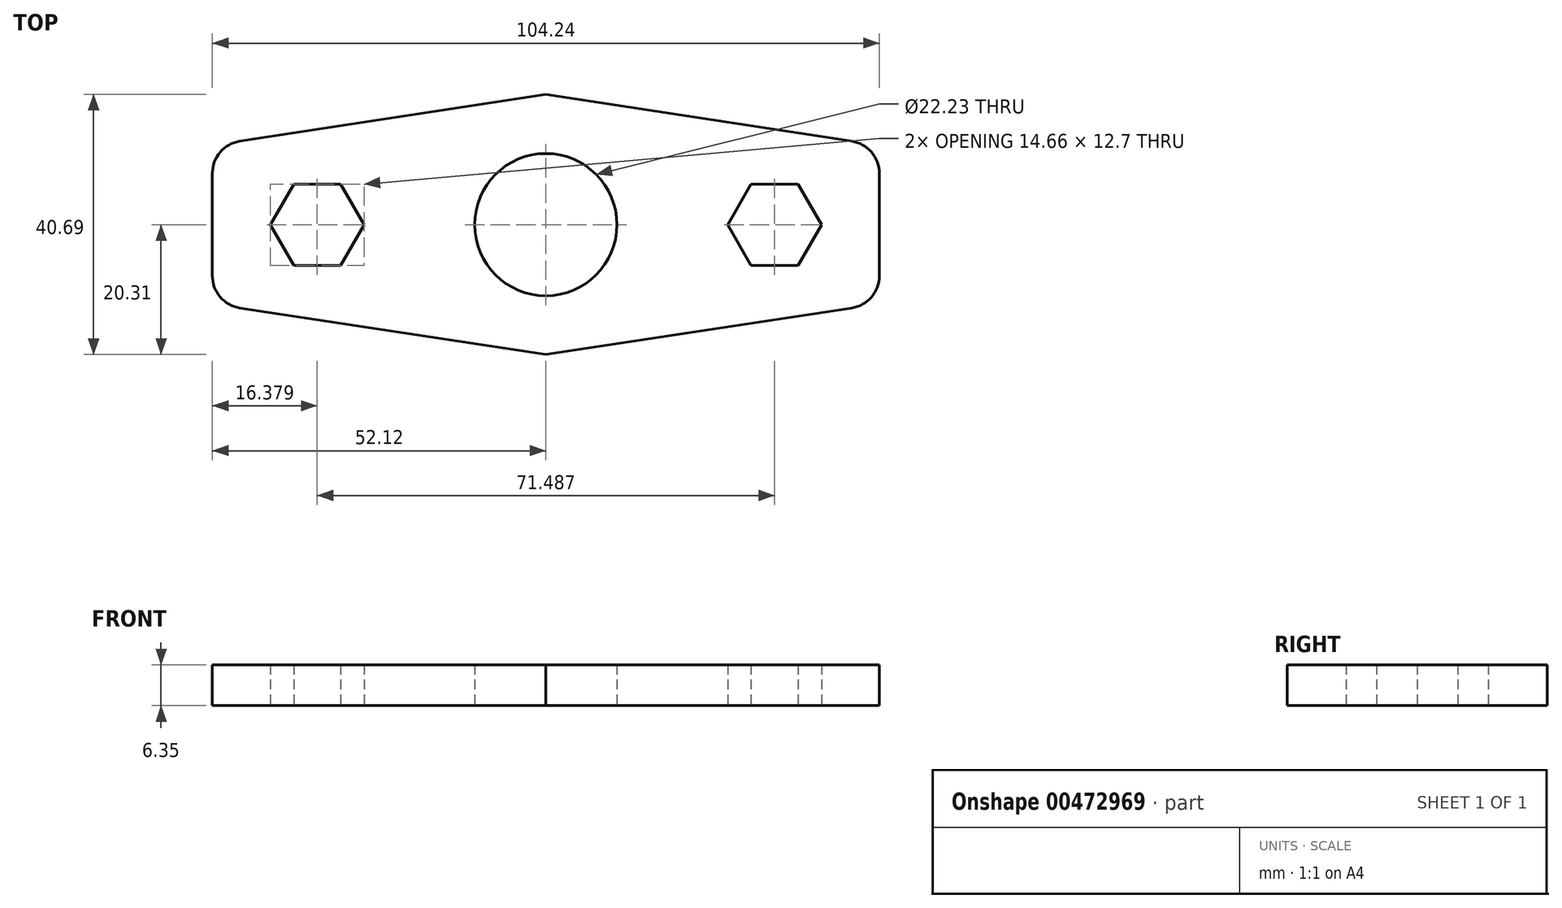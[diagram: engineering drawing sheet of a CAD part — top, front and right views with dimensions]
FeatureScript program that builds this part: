
annotation { "Feature Type Name" : "Feature", "Feature Type Description" : "" }
export const myFeature = defineFeature(function(context is Context, id is Id, definition is map)
    precondition{}
    {
        {
            var Q0;
            Q0=qCreatedBy(makeId("Top.planeOp"),FACE);
            var sketch = newSketch(context, id + "F0", { "sketchPlane" : qUnion([Q0])});
            skCircle(sketch, "E0.cCircle", {"center": v(-35.74, 0) * mm, "radius": 6.35 * mm, "construction": true});
            skLineSegment(sketch, "E0.0", {"start": v(-39.4, 6.35) * mm, "end": v(-32.08, 6.35) * mm});
            skLineSegment(sketch, "E0.1", {"start": v(-32.08, 6.35) * mm, "end": v(-28.4, 0) * mm});
            skLineSegment(sketch, "E0.2", {"start": v(-28.4, 0) * mm, "end": v(-32.08, -6.35) * mm});
            skLineSegment(sketch, "E0.3", {"start": v(-32.08, -6.35) * mm, "end": v(-39.4, -6.35) * mm});
            skLineSegment(sketch, "E0.4", {"start": v(-39.4, -6.35) * mm, "end": v(-43.07, 0) * mm});
            skLineSegment(sketch, "E0.5", {"start": v(-43.07, 0) * mm, "end": v(-39.4, 6.35) * mm});
            skPoint(sketch, "E0.0.midPoint", {"position": v(-35.74, 6.35) * mm});
            skCircle(sketch, "E1.cCircle", {"center": v(35.75, 0) * mm, "radius": 6.35 * mm, "construction": true});
            skLineSegment(sketch, "E1.0", {"start": v(32.08, 6.35) * mm, "end": v(39.41, 6.35) * mm});
            skLineSegment(sketch, "E1.1", {"start": v(39.41, 6.35) * mm, "end": v(43.08, 0) * mm});
            skLineSegment(sketch, "E1.2", {"start": v(43.08, 0) * mm, "end": v(39.41, -6.35) * mm});
            skLineSegment(sketch, "E1.3", {"start": v(39.41, -6.35) * mm, "end": v(32.08, -6.35) * mm});
            skLineSegment(sketch, "E1.4", {"start": v(32.08, -6.35) * mm, "end": v(28.41, 0) * mm});
            skLineSegment(sketch, "E1.5", {"start": v(28.41, 0) * mm, "end": v(32.08, 6.35) * mm});
            skPoint(sketch, "E1.0.midPoint", {"position": v(35.75, 6.35) * mm});
            skCircle(sketch, "E2", {"center": v(0, 0) * mm, "radius": 11.11 * mm});
            skLineSegment(sketch, "E3", {"start": v(-52.12, 12.38) * mm, "end": v(-52.12, -12.37) * mm});
            skLineSegment(sketch, "E4", {"start": v(-52.12, -12.37) * mm, "end": v(0, -20.31) * mm});
            skLineSegment(sketch, "E5", {"start": v(52.12, 12.37) * mm, "end": v(52.12, -12.37) * mm});
            skLineSegment(sketch, "E6", {"start": v(52.12, -12.37) * mm, "end": v(0, -20.31) * mm});
            skLineSegment(sketch, "E7", {"start": v(-52.12, 12.38) * mm, "end": v(0, 20.38) * mm});
            skLineSegment(sketch, "E8", {"start": v(0, 20.38) * mm, "end": v(52.12, 12.37) * mm});
            skSolve(sketch);
        }
        {
            var Q0;
            Q0=makeQuery(id+"F0.imprint","IMPRINT",FACE,{"disambiguationData":[TD([[makeQuery(id+"F0.imprint","IMPRINT",EDGE,{"derivedFrom":sQuery(id+"F0.wireOp",EDGE,"E0.0")}),1.0]])]});
            extrude(context, id + "F1", {"entities" : qUnion([Q0]), "depth" : 6.35 * mm});
        }
        {
            var Q0;
            Q0=makeQuery(id+"F1.opExtrude","SWEPT_EDGE",EDGE,{"disambiguationData":[OSD([sQuery(id+"F0.wireOp",EDGE,"E5"),sQuery(id+"F0.wireOp",EDGE,"E8")])]});
            var Q1;
            Q1=makeQuery(id+"F1.opExtrude","SWEPT_EDGE",EDGE,{"disambiguationData":[OSD([sQuery(id+"F0.wireOp",EDGE,"E5"),sQuery(id+"F0.wireOp",EDGE,"E6")])]});
            var Q2;
            Q2=makeQuery(id+"F1.opExtrude","SWEPT_EDGE",EDGE,{"disambiguationData":[OSD([sQuery(id+"F0.wireOp",EDGE,"E3"),sQuery(id+"F0.wireOp",EDGE,"E4")])]});
            var Q3;
            Q3=makeQuery(id+"F1.opExtrude","SWEPT_EDGE",EDGE,{"disambiguationData":[OSD([sQuery(id+"F0.wireOp",EDGE,"E3"),sQuery(id+"F0.wireOp",EDGE,"E7")])]});
            fillet(context, id + "F2", {"entities" : qUnion([Q0, Q1, Q2, Q3]), "radius" : 5.08 * mm, "tangentPropagation" : true, "allowEdgeOverflow" : false});
        }
    });
